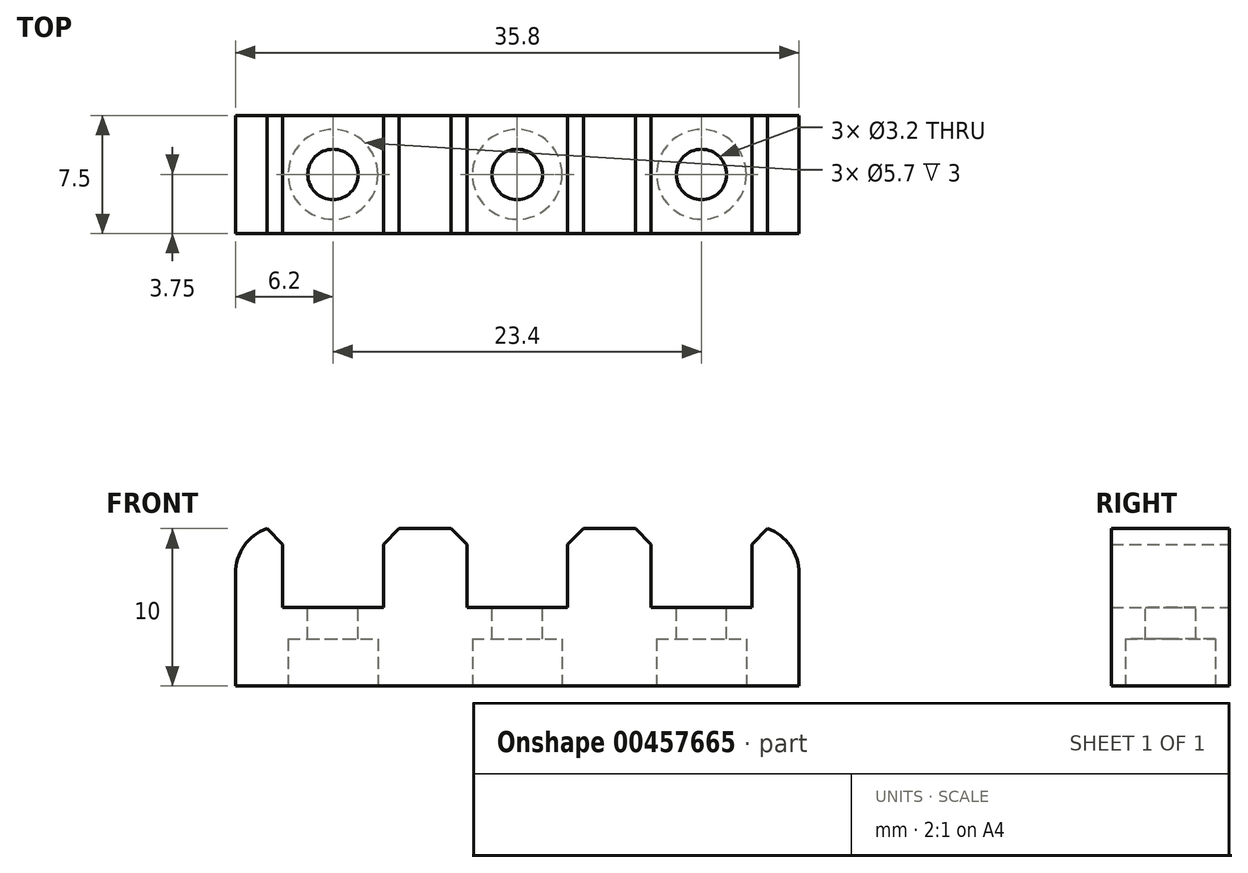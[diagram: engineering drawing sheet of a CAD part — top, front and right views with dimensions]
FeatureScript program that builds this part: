
annotation { "Feature Type Name" : "Feature", "Feature Type Description" : "" }
export const myFeature = defineFeature(function(context is Context, id is Id, definition is map)
    precondition{}
    {
        {
            var Q0;
            Q0=qCreatedBy(makeId("Front.planeOp"),FACE);
            var sketch = newSketch(context, id + "F0", { "sketchPlane" : qUnion([Q0])});
            skLineSegment(sketch, "E0", {"start": v(0, 0) * mm, "end": v(0, 10) * mm});
            skLineSegment(sketch, "E1", {"start": v(0, 10) * mm, "end": v(3, 10) * mm});
            skLineSegment(sketch, "E2", {"start": v(3, 10) * mm, "end": v(3, 5) * mm});
            skLineSegment(sketch, "E3", {"start": v(3, 5) * mm, "end": v(9.4, 5) * mm});
            skLineSegment(sketch, "E4", {"start": v(9.4, 5) * mm, "end": v(9.4, 10) * mm});
            skLineSegment(sketch, "E5", {"start": v(9.4, 10) * mm, "end": v(14.7, 10) * mm});
            skLineSegment(sketch, "E6", {"start": v(14.7, 10) * mm, "end": v(14.7, 5) * mm});
            skLineSegment(sketch, "E7", {"start": v(14.7, 5) * mm, "end": v(21.1, 5) * mm});
            skLineSegment(sketch, "E8", {"start": v(21.1, 5) * mm, "end": v(21.1, 10) * mm});
            skLineSegment(sketch, "E9", {"start": v(21.1, 10) * mm, "end": v(26.4, 10) * mm});
            skLineSegment(sketch, "E10", {"start": v(26.4, 10) * mm, "end": v(26.4, 5) * mm});
            skLineSegment(sketch, "E11", {"start": v(26.4, 5) * mm, "end": v(32.8, 5) * mm});
            skLineSegment(sketch, "E12", {"start": v(32.8, 5) * mm, "end": v(32.8, 10) * mm});
            skLineSegment(sketch, "E13", {"start": v(32.8, 10) * mm, "end": v(35.8, 10) * mm});
            skLineSegment(sketch, "E14", {"start": v(35.8, 10) * mm, "end": v(35.8, 0) * mm});
            skLineSegment(sketch, "E15", {"start": v(35.8, 0) * mm, "end": v(0, 0) * mm});
            skSolve(sketch);
        }
        {
            var Q0;
            Q0=makeQuery(id+"F0.imprint","IMPRINT",FACE,{"disambiguationData":[TD([[makeQuery(id+"F0.imprint","IMPRINT",EDGE,{"derivedFrom":sQuery(id+"F0.wireOp",EDGE,"E0")}),-1.0]])]});
            extrude(context, id + "F1", {"entities" : qUnion([Q0]), "depth" : 7.5 * mm});
        }
        {
            var Q0;
            Q0=makeQuery(id+"F1.opExtrude","SWEPT_EDGE",EDGE,{"disambiguationData":[OSD([sQuery(id+"F0.wireOp",EDGE,"E1"),sQuery(id+"F0.wireOp",EDGE,"E2")])]});
            var Q1;
            Q1=makeQuery(id+"F1.opExtrude","SWEPT_EDGE",EDGE,{"disambiguationData":[OSD([sQuery(id+"F0.wireOp",EDGE,"E4"),sQuery(id+"F0.wireOp",EDGE,"E5")])]});
            var Q2;
            Q2=makeQuery(id+"F1.opExtrude","SWEPT_EDGE",EDGE,{"disambiguationData":[OSD([sQuery(id+"F0.wireOp",EDGE,"E5"),sQuery(id+"F0.wireOp",EDGE,"E6")])]});
            var Q3;
            Q3=makeQuery(id+"F1.opExtrude","SWEPT_EDGE",EDGE,{"disambiguationData":[OSD([sQuery(id+"F0.wireOp",EDGE,"E8"),sQuery(id+"F0.wireOp",EDGE,"E9")])]});
            var Q4;
            Q4=makeQuery(id+"F1.opExtrude","SWEPT_EDGE",EDGE,{"disambiguationData":[OSD([sQuery(id+"F0.wireOp",EDGE,"E9"),sQuery(id+"F0.wireOp",EDGE,"E10")])]});
            var Q5;
            Q5=makeQuery(id+"F1.opExtrude","SWEPT_EDGE",EDGE,{"disambiguationData":[OSD([sQuery(id+"F0.wireOp",EDGE,"E12"),sQuery(id+"F0.wireOp",EDGE,"E13")])]});
            chamfer(context, id + "F2", {"entities" : qUnion([Q0, Q1, Q2, Q3, Q4, Q5]), "width" : 1 * mm, "tangentPropagation" : true});
        }
        {
            var Q0;
            Q0=makeQuery(id+"F1.opExtrude","SWEPT_EDGE",EDGE,{"disambiguationData":[OSD([sQuery(id+"F0.wireOp",EDGE,"E0"),sQuery(id+"F0.wireOp",EDGE,"E1")])]});
            var Q1;
            Q1=makeQuery(id+"F1.opExtrude","SWEPT_EDGE",EDGE,{"disambiguationData":[OSD([sQuery(id+"F0.wireOp",EDGE,"E13"),sQuery(id+"F0.wireOp",EDGE,"E14")])]});
            fillet(context, id + "F3", {"entities" : qUnion([Q0, Q1]), "radius" : 3 * mm, "tangentPropagation" : true, "allowEdgeOverflow" : false});
        }
        {
            var Q0;
            Q0=makeQuery(id+"F1.opExtrude","SWEPT_FACE",FACE,{"disambiguationData":[OSD([sQuery(id+"F0.wireOp",EDGE,"E3")])]});
            var sketch = newSketch(context, id + "F4", { "sketchPlane" : qUnion([Q0])});
            skCircle(sketch, "E16", {"center": v(6.2, -3.75) * mm, "radius": 1.6 * mm});
            skSolve(sketch);
        }
        {
            var Q0;
            Q0=makeQuery(id+"F4.imprint","IMPRINT",FACE,{"disambiguationData":[TD([[makeQuery(id+"F4.imprint","IMPRINT",EDGE,{"derivedFrom":sQuery(id+"F4.wireOp",EDGE,"E16")}),1.0]])]});
            extrude(context, id + "F5", {"entities" : qUnion([Q0]), "operationType" : NewBodyOperationType.REMOVE, "endBound" : BoundingType.THROUGH_ALL, "oppositeDirection" : true, "depth" : 25 * mm});
        }
        {
            var Q0;
            Q0=makeQuery(id+"F1.opExtrude","SWEPT_FACE",FACE,{"disambiguationData":[OSD([sQuery(id+"F0.wireOp",EDGE,"E7")])]});
            var sketch = newSketch(context, id + "F6", { "sketchPlane" : qUnion([Q0])});
            skCircle(sketch, "E17", {"center": v(17.9, -3.75) * mm, "radius": 1.6 * mm});
            skSolve(sketch);
        }
        {
            var Q0;
            Q0=makeQuery(id+"F6.imprint","IMPRINT",FACE,{"disambiguationData":[TD([[makeQuery(id+"F6.imprint","IMPRINT",EDGE,{"derivedFrom":sQuery(id+"F6.wireOp",EDGE,"E17")}),1.0]])]});
            extrude(context, id + "F7", {"entities" : qUnion([Q0]), "operationType" : NewBodyOperationType.REMOVE, "endBound" : BoundingType.THROUGH_ALL, "oppositeDirection" : true, "depth" : 25 * mm});
        }
        {
            var Q0;
            Q0=makeQuery(id+"F1.opExtrude","SWEPT_FACE",FACE,{"disambiguationData":[OSD([sQuery(id+"F0.wireOp",EDGE,"E11")])]});
            var sketch = newSketch(context, id + "F8", { "sketchPlane" : qUnion([Q0])});
            skCircle(sketch, "E18", {"center": v(29.6, -3.75) * mm, "radius": 1.6 * mm});
            skSolve(sketch);
        }
        {
            var Q0;
            Q0=makeQuery(id+"F8.imprint","IMPRINT",FACE,{"disambiguationData":[TD([[makeQuery(id+"F8.imprint","IMPRINT",EDGE,{"derivedFrom":sQuery(id+"F8.wireOp",EDGE,"E18")}),1.0]])]});
            extrude(context, id + "F9", {"entities" : qUnion([Q0]), "operationType" : NewBodyOperationType.REMOVE, "endBound" : BoundingType.THROUGH_ALL, "oppositeDirection" : true, "depth" : 25 * mm});
        }
        {
            var Q0;
            Q0=makeQuery(id+"F1.opExtrude","SWEPT_FACE",FACE,{"disambiguationData":[OSD([sQuery(id+"F0.wireOp",EDGE,"E15")])]});
            var sketch = newSketch(context, id + "F10", { "sketchPlane" : qUnion([Q0])});
            skCircle(sketch, "E19", {"center": v(6.2, 3.75) * mm, "radius": 2.85 * mm});
            skCircle(sketch, "E20", {"center": v(17.9, 3.75) * mm, "radius": 2.85 * mm});
            skCircle(sketch, "E21", {"center": v(29.6, 3.75) * mm, "radius": 2.85 * mm});
            skSolve(sketch);
        }
        {
            var Q0;
            Q0=makeQuery(id+"F10.imprint","IMPRINT",FACE,{"disambiguationData":[TD([[makeQuery(id+"F10.imprint","IMPRINT",EDGE,{"derivedFrom":sQuery(id+"F10.wireOp",EDGE,"E19")}),1.0]])]});
            var Q1;
            Q1=makeQuery(id+"F10.imprint","IMPRINT",FACE,{"disambiguationData":[TD([[makeQuery(id+"F10.imprint","IMPRINT",EDGE,{"derivedFrom":sQuery(id+"F10.wireOp",EDGE,"E20")}),1.0]])]});
            var Q2;
            Q2=makeQuery(id+"F10.imprint","IMPRINT",FACE,{"disambiguationData":[TD([[makeQuery(id+"F10.imprint","IMPRINT",EDGE,{"derivedFrom":sQuery(id+"F10.wireOp",EDGE,"E21")}),1.0]])]});
            extrude(context, id + "F11", {"entities" : qUnion([Q0, Q1, Q2]), "operationType" : NewBodyOperationType.REMOVE, "oppositeDirection" : true, "depth" : 3 * mm});
        }
    });
